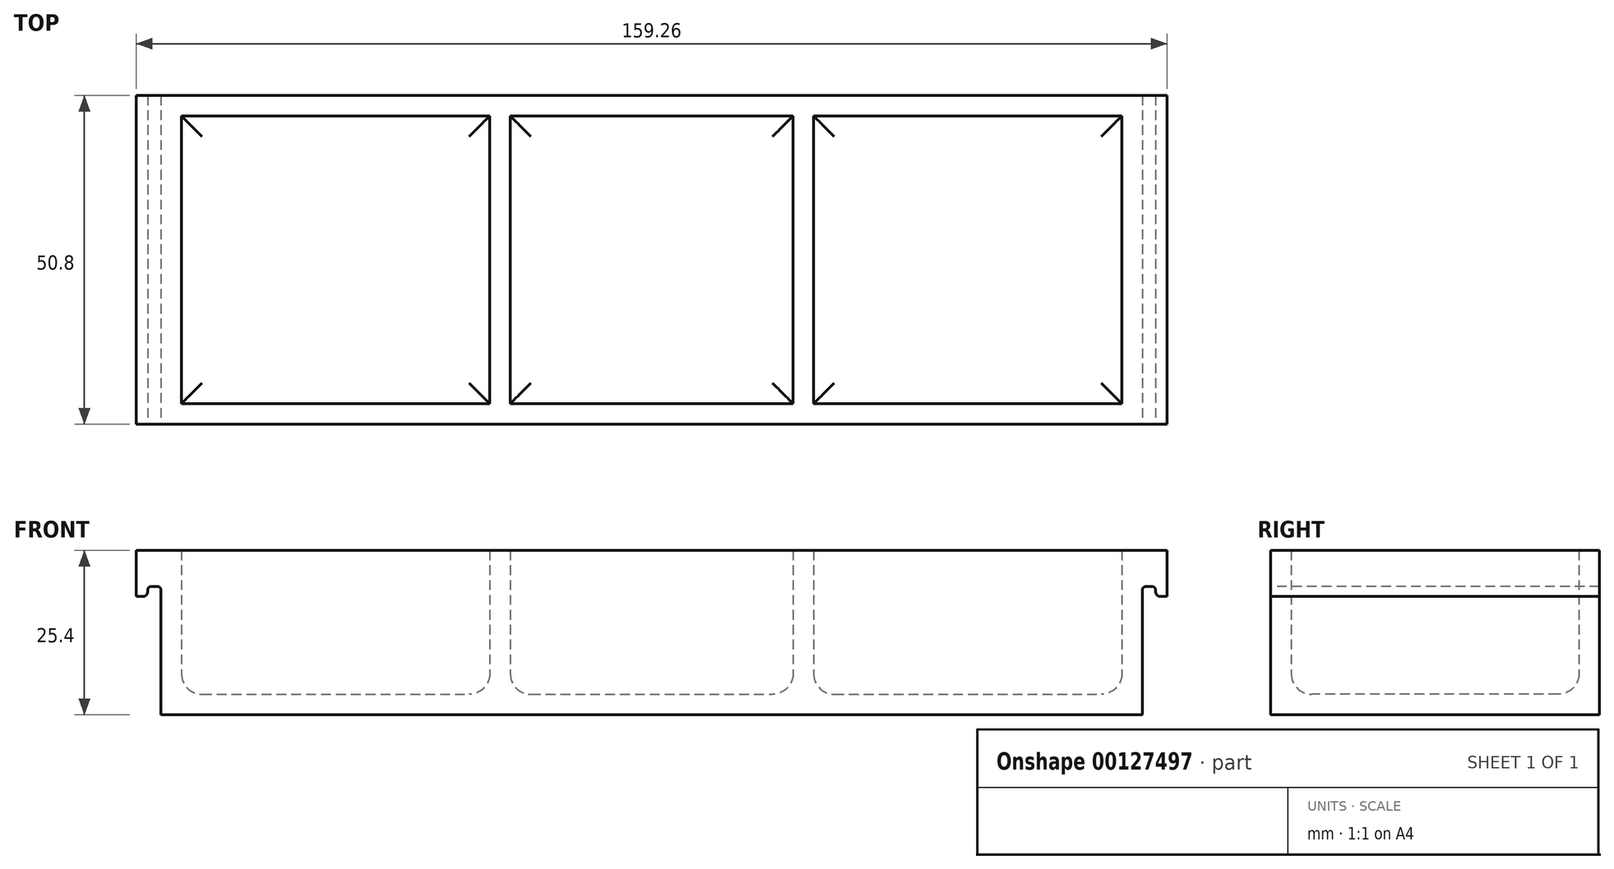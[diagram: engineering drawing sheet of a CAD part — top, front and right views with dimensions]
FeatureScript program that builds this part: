
annotation { "Feature Type Name" : "Feature", "Feature Type Description" : "" }
export const myFeature = defineFeature(function(context is Context, id is Id, definition is map)
    precondition{}
    {
        {
            var Q0;
            Q0=qCreatedBy(makeId("Front.planeOp"),FACE);
            var sketch = newSketch(context, id + "F0", { "sketchPlane" : qUnion([Q0])});
            skLineSegment(sketch, "E0.bottom", {"start": v(-79.63, 0) * mm, "end": v(79.63, 0) * mm});
            skLineSegment(sketch, "E0.top", {"start": v(-79.63, -25.4) * mm, "end": v(79.63, -25.4) * mm});
            skLineSegment(sketch, "E0.left", {"start": v(-79.63, 0) * mm, "end": v(-79.63, -25.4) * mm});
            skLineSegment(sketch, "E0.right", {"start": v(79.63, 0) * mm, "end": v(79.63, -25.4) * mm});
            skSolve(sketch);
        }
        {
            var Q0;
            Q0 = qSketchRegion(id + "F0", true);
            extrude(context, id + "F1", {"entities" : qUnion([Q0]), "oppositeDirection" : true, "depth" : 50.8 * mm});
        }
        {
            var Q0;
            Q0=makeQuery(id+"F1.opExtrude","CAP_FACE",FACE,{"disambiguationData":[OSD([sQuery(id+"F0.wireOp",EDGE,"E0.bottom"),sQuery(id+"F0.wireOp",EDGE,"E0.top"),sQuery(id+"F0.wireOp",EDGE,"E0.left"),sQuery(id+"F0.wireOp",EDGE,"E0.right")])],"isStart":true});
            var sketch = newSketch(context, id + "F2", { "sketchPlane" : qUnion([Q0])});
            skLineSegment(sketch, "E1", {"start": v(-79.63, -7.11) * mm, "end": v(-77.85, -7.11) * mm});
            skLineSegment(sketch, "E2", {"start": v(-77.85, -7.11) * mm, "end": v(-77.85, -5.59) * mm});
            skLineSegment(sketch, "E3", {"start": v(-77.85, -5.59) * mm, "end": v(-75.82, -5.59) * mm});
            skLineSegment(sketch, "E4", {"start": v(-75.82, -5.59) * mm, "end": v(-75.82, -25.4) * mm});
            skLineSegment(sketch, "E5", {"start": v(-75.82, -25.4) * mm, "end": v(-79.63, -25.4) * mm});
            skLineSegment(sketch, "E6", {"start": v(-79.63, -25.4) * mm, "end": v(-79.63, -7.11) * mm});
            skLineSegment(sketch, "E7.MirrorCS", {"start": v(75.82, -5.59) * mm, "end": v(75.82, -25.4) * mm});
            skLineSegment(sketch, "E8.MirrorCS", {"start": v(79.63, -25.4) * mm, "end": v(79.63, -7.11) * mm});
            skLineSegment(sketch, "E9.MirrorCS", {"start": v(75.82, -25.4) * mm, "end": v(79.63, -25.4) * mm});
            skLineSegment(sketch, "E10.MirrorCS", {"start": v(77.85, -5.59) * mm, "end": v(75.82, -5.59) * mm});
            skLineSegment(sketch, "E11.MirrorCS", {"start": v(77.85, -7.11) * mm, "end": v(77.85, -5.59) * mm});
            skLineSegment(sketch, "E12.MirrorCS", {"start": v(79.63, -7.11) * mm, "end": v(77.85, -7.11) * mm});
            skSolve(sketch);
        }
        {
            var Q0;
            Q0 = qSketchRegion(id + "F2", true);
            extrude(context, id + "F3", {"entities" : qUnion([Q0]), "operationType" : NewBodyOperationType.REMOVE, "endBound" : BoundingType.THROUGH_ALL, "oppositeDirection" : true, "depth" : 25.4 * mm});
        }
        {
            var Q0;
            Q0=makeQuery(id+"F3.boolean.opBoolean","COPY",EDGE,{"derivedFrom":makeQuery(id+"F3.opExtrude","SWEPT_EDGE",EDGE,{"disambiguationData":[OSD([sQuery(id+"F0.wireOp",EDGE,"E0.left"),sQuery(id+"F2.wireOp",EDGE,"E1"),sQuery(id+"F2.wireOp",EDGE,"E6")])]})});
            var Q1;
            Q1=makeQuery(id+"F3.boolean.opBoolean","COPY",EDGE,{"derivedFrom":makeQuery(id+"F3.opExtrude","SWEPT_EDGE",EDGE,{"disambiguationData":[OSD([sQuery(id+"F2.wireOp",EDGE,"E1"),sQuery(id+"F2.wireOp",EDGE,"E2")])]})});
            var Q2;
            Q2=makeQuery(id+"F3.boolean.opBoolean","COPY",EDGE,{"derivedFrom":makeQuery(id+"F3.opExtrude","SWEPT_EDGE",EDGE,{"disambiguationData":[OSD([sQuery(id+"F2.wireOp",EDGE,"E11.MirrorCS"),sQuery(id+"F2.wireOp",EDGE,"E12.MirrorCS")])]})});
            var Q3;
            Q3=makeQuery(id+"F3.boolean.opBoolean","COPY",EDGE,{"derivedFrom":makeQuery(id+"F3.opExtrude","SWEPT_EDGE",EDGE,{"disambiguationData":[OSD([sQuery(id+"F0.wireOp",EDGE,"E0.right"),sQuery(id+"F2.wireOp",EDGE,"E8.MirrorCS"),sQuery(id+"F2.wireOp",EDGE,"E12.MirrorCS")])]})});
            fillet(context, id + "F4", {"entities" : qUnion([Q0, Q1, Q2, Q3]), "radius" : 0.76 * mm, "tangentPropagation" : true, "allowEdgeOverflow" : false});
        }
        {
            var Q0;
            Q0=makeQuery(id+"F3.boolean.opBoolean","COPY",EDGE,{"derivedFrom":makeQuery(id+"F3.opExtrude","SWEPT_EDGE",EDGE,{"disambiguationData":[OSD([sQuery(id+"F2.wireOp",EDGE,"E2"),sQuery(id+"F2.wireOp",EDGE,"E3")])]})});
            var Q1;
            Q1=makeQuery(id+"F3.boolean.opBoolean","COPY",EDGE,{"derivedFrom":makeQuery(id+"F3.opExtrude","SWEPT_EDGE",EDGE,{"disambiguationData":[OSD([sQuery(id+"F2.wireOp",EDGE,"E3"),sQuery(id+"F2.wireOp",EDGE,"E4")])]})});
            var Q2;
            Q2=makeQuery(id+"F3.boolean.opBoolean","COPY",EDGE,{"derivedFrom":makeQuery(id+"F3.opExtrude","SWEPT_EDGE",EDGE,{"disambiguationData":[OSD([sQuery(id+"F2.wireOp",EDGE,"E10.MirrorCS"),sQuery(id+"F2.wireOp",EDGE,"E11.MirrorCS")])]})});
            var Q3;
            Q3=makeQuery(id+"F3.boolean.opBoolean","COPY",EDGE,{"derivedFrom":makeQuery(id+"F3.opExtrude","SWEPT_EDGE",EDGE,{"disambiguationData":[OSD([sQuery(id+"F2.wireOp",EDGE,"E7.MirrorCS"),sQuery(id+"F2.wireOp",EDGE,"E10.MirrorCS")])]})});
            fillet(context, id + "F5", {"entities" : qUnion([Q0, Q1, Q2, Q3]), "radius" : 0.5 * mm, "tangentPropagation" : true, "allowEdgeOverflow" : false});
        }
        {
            var Q0;
            Q0=makeQuery(id+"F1.opExtrude","SWEPT_FACE",FACE,{"disambiguationData":[OSD([sQuery(id+"F0.wireOp",EDGE,"E0.top")])]});
            cPlane(context, id + "F6", {"entities" : qUnion([Q0]), "cplaneType" : CPlaneType.OFFSET, "offset" : 3.17 * mm, "oppositeDirection" : true, "width" : 152.4 * mm, "height" : 152.4 * mm});
        }
        {
            var Q0;
            Q0=qCreatedBy(id+"F6.planeOp",FACE);
            var sketch = newSketch(context, id + "F7", { "sketchPlane" : qUnion([Q0])});
            skLineSegment(sketch, "E13.bottom", {"start": v(-72.64, -3.17) * mm, "end": v(72.64, -3.17) * mm});
            skLineSegment(sketch, "E13.top", {"start": v(-72.64, -47.63) * mm, "end": v(72.64, -47.63) * mm});
            skLineSegment(sketch, "E13.left", {"start": v(-72.64, -3.17) * mm, "end": v(-72.64, -47.63) * mm});
            skLineSegment(sketch, "E13.right", {"start": v(72.64, -3.17) * mm, "end": v(72.64, -47.63) * mm});
            skSolve(sketch);
        }
        {
            var Q0;
            Q0 = qSketchRegion(id + "F7", true);
            extrude(context, id + "F8", {"entities" : qUnion([Q0]), "operationType" : NewBodyOperationType.REMOVE, "endBound" : BoundingType.THROUGH_ALL, "oppositeDirection" : true, "depth" : 25.4 * mm});
        }
        {
            var Q0;
            Q0=makeQuery(id+"F8.boolean.opBoolean","COPY",FACE,{"derivedFrom":makeQuery(id+"F8.opExtrude","CAP_FACE",FACE,{"disambiguationData":[OSD([sQuery(id+"F7.wireOp",EDGE,"E13.bottom"),sQuery(id+"F7.wireOp",EDGE,"E13.top"),sQuery(id+"F7.wireOp",EDGE,"E13.left"),sQuery(id+"F7.wireOp",EDGE,"E13.right")])],"isStart":true})});
            var sketch = newSketch(context, id + "F9", { "sketchPlane" : qUnion([Q0])});
            skLineSegment(sketch, "E14.bottom", {"start": v(-25.02, 47.63) * mm, "end": v(-21.84, 47.63) * mm});
            skLineSegment(sketch, "E14.top", {"start": v(-25.02, 3.17) * mm, "end": v(-21.84, 3.17) * mm});
            skLineSegment(sketch, "E14.left", {"start": v(-25.02, 47.63) * mm, "end": v(-25.02, 3.17) * mm});
            skLineSegment(sketch, "E14.right", {"start": v(-21.84, 47.63) * mm, "end": v(-21.84, 3.17) * mm});
            skLineSegment(sketch, "E15.bottom", {"start": v(25.02, 47.63) * mm, "end": v(21.84, 47.63) * mm});
            skLineSegment(sketch, "E15.top", {"start": v(25.02, 3.17) * mm, "end": v(21.84, 3.17) * mm});
            skLineSegment(sketch, "E15.left", {"start": v(25.02, 47.63) * mm, "end": v(25.02, 3.17) * mm});
            skLineSegment(sketch, "E15.right", {"start": v(21.84, 47.63) * mm, "end": v(21.84, 3.17) * mm});
            skSolve(sketch);
        }
        {
            var Q0;
            Q0 = qSketchRegion(id + "F9", true);
            var Q1;
            Q1=makeQuery(id+"F1.opExtrude","SWEPT_FACE",FACE,{"disambiguationData":[OSD([sQuery(id+"F0.wireOp",EDGE,"E0.bottom")])]});
            extrude(context, id + "F10", {"entities" : qUnion([Q0]), "operationType" : NewBodyOperationType.ADD, "endBound" : BoundingType.UP_TO_SURFACE, "endBoundEntityFace" : qUnion([Q1]), "depth" : 25.4 * mm});
        }
        {
            var Q0;
            {var subQ0=sQuery(id+"F7.wireOp",EDGE,"E13.bottom");var subQ1=sQuery(id+"F7.wireOp",EDGE,"E13.top");var subQ2=sQuery(id+"F7.wireOp",EDGE,"E13.left");Q0=makeQuery(id+"F10.boolean.opBoolean","SPLIT",FACE,{"disambiguationData":[TD([makeQuery(id+"F8.boolean.opBoolean","COPY",FACE,{"derivedFrom":makeQuery(id+"F8.opExtrude","SWEPT_FACE",FACE,{"disambiguationData":[OSD([subQ2])]})})])],"derivedFrom":makeQuery(id+"F8.boolean.opBoolean","COPY",FACE,{"derivedFrom":makeQuery(id+"F8.opExtrude","CAP_FACE",FACE,{"disambiguationData":[OSD([subQ0,subQ1,subQ2,sQuery(id+"F7.wireOp",EDGE,"E13.right")])],"isStart":true})})});}
            var Q1;
            {var subQ0=sQuery(id+"F7.wireOp",EDGE,"E13.bottom");var subQ1=sQuery(id+"F7.wireOp",EDGE,"E13.top");Q1=makeQuery(id+"F10.boolean.opBoolean","SPLIT",FACE,{"disambiguationData":[TD([makeQuery(id+"F10.opExtrude","SWEPT_FACE",FACE,{"disambiguationData":[OSD([sQuery(id+"F9.wireOp",EDGE,"E14.right")])]})])],"derivedFrom":makeQuery(id+"F8.boolean.opBoolean","COPY",FACE,{"derivedFrom":makeQuery(id+"F8.opExtrude","CAP_FACE",FACE,{"disambiguationData":[OSD([subQ0,subQ1,sQuery(id+"F7.wireOp",EDGE,"E13.left"),sQuery(id+"F7.wireOp",EDGE,"E13.right")])],"isStart":true})})});}
            var Q2;
            {var subQ0=sQuery(id+"F7.wireOp",EDGE,"E13.bottom");var subQ1=sQuery(id+"F7.wireOp",EDGE,"E13.top");var subQ2=sQuery(id+"F7.wireOp",EDGE,"E13.right");Q2=makeQuery(id+"F10.boolean.opBoolean","SPLIT",FACE,{"disambiguationData":[TD([makeQuery(id+"F8.boolean.opBoolean","COPY",FACE,{"derivedFrom":makeQuery(id+"F8.opExtrude","SWEPT_FACE",FACE,{"disambiguationData":[OSD([subQ2])]})})])],"derivedFrom":makeQuery(id+"F8.boolean.opBoolean","COPY",FACE,{"derivedFrom":makeQuery(id+"F8.opExtrude","CAP_FACE",FACE,{"disambiguationData":[OSD([subQ0,subQ1,sQuery(id+"F7.wireOp",EDGE,"E13.left"),subQ2])],"isStart":true})})});}
            fillet(context, id + "F11", {"entities" : qUnion([Q0, Q1, Q2]), "radius" : 3.17 * mm, "tangentPropagation" : true, "allowEdgeOverflow" : false});
        }
    });
